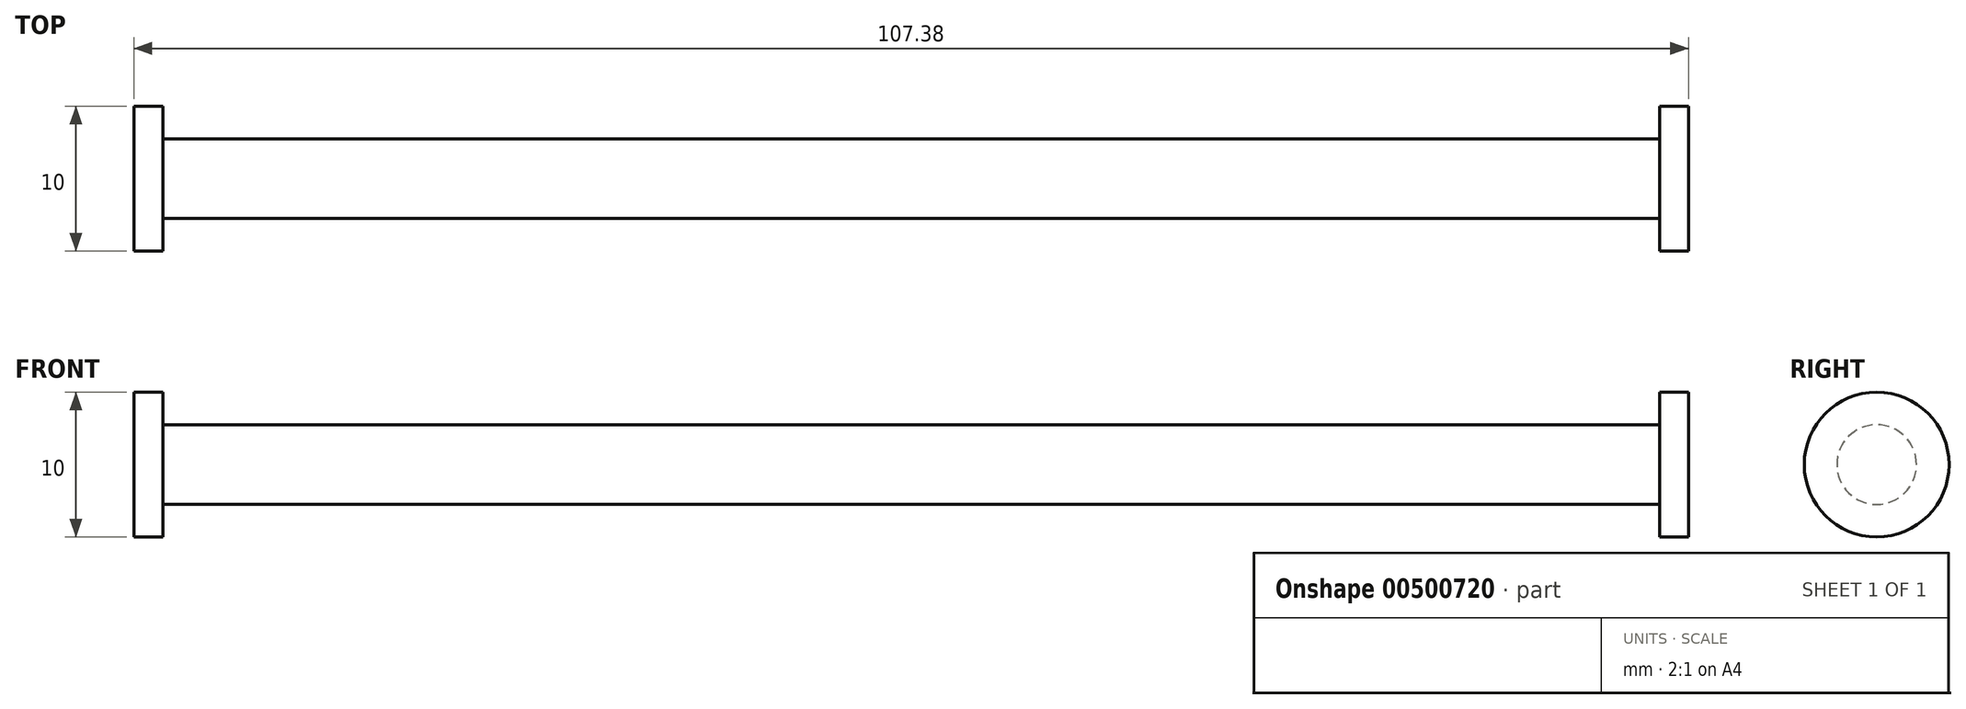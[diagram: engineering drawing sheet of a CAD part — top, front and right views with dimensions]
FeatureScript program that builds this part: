
annotation { "Feature Type Name" : "Feature", "Feature Type Description" : "" }
export const myFeature = defineFeature(function(context is Context, id is Id, definition is map)
    precondition{}
    {
        {
            var Q0;
            Q0=qCreatedBy(makeId("Right.planeOp"),FACE);
            var sketch = newSketch(context, id + "F0", { "sketchPlane" : qUnion([Q0])});
            skCircle(sketch, "E0", {"center": v(0, 0) * mm, "radius": 2.75 * mm});
            skSolve(sketch);
        }
        {
            var Q0;
            Q0 = qSketchRegion(id + "F0", true);
            extrude(context, id + "F1", {"entities" : qUnion([Q0]), "depth" : 103.38 * mm, "offsetDistance" : 25 * mm});
        }
        {
            var Q0;
            Q0=qCreatedBy(makeId("Right.planeOp"),FACE);
            var sketch = newSketch(context, id + "F2", { "sketchPlane" : qUnion([Q0])});
            skCircle(sketch, "E1", {"center": v(0, 0) * mm, "radius": 5 * mm});
            skSolve(sketch);
        }
        {
            var Q0;
            Q0 = qSketchRegion(id + "F2", true);
            extrude(context, id + "F3", {"entities" : qUnion([Q0]), "operationType" : NewBodyOperationType.ADD, "oppositeDirection" : true, "depth" : 2 * mm, "offsetDistance" : 25 * mm});
        }
        {
            var Q0;
            Q0=qCreatedBy(makeId("Right.planeOp"),FACE);
            cPlane(context, id + "F4", {"entities" : qUnion([Q0]), "cplaneType" : CPlaneType.OFFSET, "offset" : 103.38 * mm, "width" : 150 * mm, "height" : 150 * mm});
        }
        {
            var Q0;
            Q0=qCreatedBy(id+"F4.planeOp",FACE);
            var sketch = newSketch(context, id + "F5", { "sketchPlane" : qUnion([Q0])});
            skCircle(sketch, "E2", {"center": v(0, 0) * mm, "radius": 5 * mm});
            skSolve(sketch);
        }
        {
            var Q0;
            Q0 = qSketchRegion(id + "F5", true);
            extrude(context, id + "F6", {"entities" : qUnion([Q0]), "operationType" : NewBodyOperationType.ADD, "depth" : 2 * mm, "offsetDistance" : 25 * mm});
        }
    });
